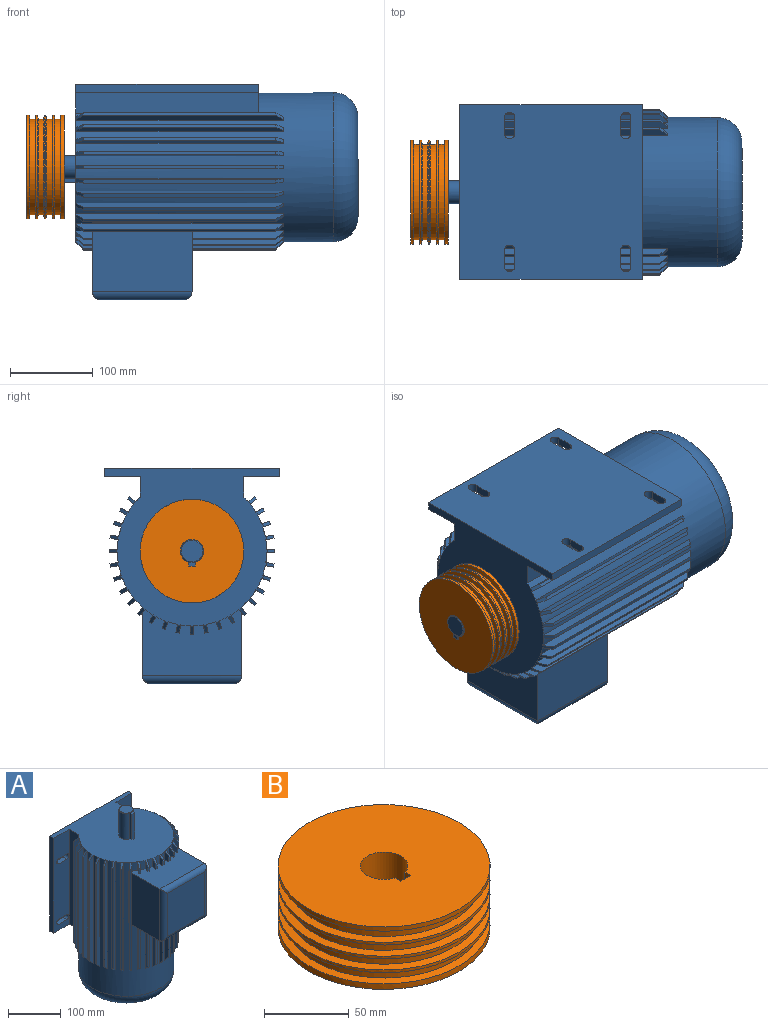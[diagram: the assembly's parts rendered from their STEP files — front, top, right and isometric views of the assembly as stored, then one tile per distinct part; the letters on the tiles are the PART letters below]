
ASSEMBLY  parts=2 mates=1
PART A: 242 faces, bbox 210.4x260.4x400.4 mm
  f0: plane 250x7.66mm, normal (0.77,-0.64,0), area 1729.1mm2, adj f30,f31,f53,f54,f55,f56,f57,f234
  f1: plane 250x7.66mm, normal (-0.77,-0.64,0), area 1729.1mm2, adj f2,f31,f54,f58,f59,f60,f61,f235
  f2: cylinder r=90mm len=20mm, axis (0,0,1), area 234.2mm2, adj f1,f3,f54,f235
  f3: plane 20x8.66mm, normal (0.87,0.5,0), area 159.5mm2, adj f2,f4,f54,f62,f235
  f4: plane 11x3.46mm, normal (0.5,-0.87,0), area 44mm2, adj f3,f5,f62,f235
  f5: plane 20x8.66mm, normal (-0.87,-0.5,0), area 159.5mm2, adj f4,f6,f54,f62,f235
  f6: cylinder r=90mm len=20mm, axis (0,0,1), area 234.2mm2, adj f5,f7,f54,f235
  f7: plane 20x9.4mm, normal (0.94,0.34,0), area 159.5mm2, adj f6,f8,f54,f63,f235
  f8: plane 11x3.76mm, normal (0.34,-0.94,0), area 44mm2, adj f7,f9,f63,f235
  f9: plane 20x9.4mm, normal (-0.94,-0.34,0), area 159.5mm2, adj f8,f10,f54,f63,f235
  f10: cylinder r=90mm len=20mm, axis (0,0,1), area 234.2mm2, adj f9,f11,f54,f235
  f11: plane 20x9.85mm, normal (0.98,0.17,0), area 159.5mm2, adj f10,f12,f54,f64,f235
  f12: plane 11x3.94mm, normal (0.17,-0.98,0), area 44mm2, adj f11,f13,f64,f235
  f13: plane 20x9.85mm, normal (-0.98,-0.17,0), area 159.5mm2, adj f12,f14,f54,f64,f235
  f14: cylinder r=90mm len=20mm, axis (0,0,1), area 234.2mm2, adj f13,f15,f54,f235
  f15: plane 20x10mm, normal (1,0,0), area 159.5mm2, adj f14,f16,f54,f65,f235
  f16: plane 11x4mm, normal (0,-1,0), area 44mm2, adj f15,f17,f65,f235
  f17: plane 20x10mm, normal (-1,0,0), area 159.5mm2, adj f16,f18,f54,f65,f235
  f18: cylinder r=90mm len=20mm, axis (0,0,1), area 234.2mm2, adj f17,f19,f54,f235
  f19: plane 20x9.85mm, normal (0.98,-0.17,0), area 159.5mm2, adj f18,f20,f54,f66,f235
  f20: plane 11x3.94mm, normal (-0.17,-0.98,0), area 44mm2, adj f19,f21,f66,f235
  f21: plane 20x9.85mm, normal (-0.98,0.17,0), area 159.5mm2, adj f20,f22,f54,f66,f235
  f22: cylinder r=90mm len=20mm, axis (0,0,1), area 234.2mm2, adj f21,f23,f54,f235
  f23: plane 20x9.4mm, normal (0.94,-0.34,0), area 159.5mm2, adj f22,f24,f54,f67,f235
  f24: plane 11x3.76mm, normal (-0.34,-0.94,0), area 44mm2, adj f23,f25,f67,f235
  f25: plane 20x9.4mm, normal (-0.94,0.34,0), area 159.5mm2, adj f24,f26,f54,f67,f235
  f26: cylinder r=90mm len=20mm, axis (0,0,1), area 234.2mm2, adj f25,f27,f54,f235
  f27: plane 20x8.66mm, normal (0.87,-0.5,0), area 159.5mm2, adj f26,f28,f54,f68,f235
  f28: plane 11x3.46mm, normal (-0.5,-0.87,0), area 44mm2, adj f27,f29,f68,f235
  f29: plane 20x8.66mm, normal (-0.87,0.5,0), area 159.5mm2, adj f28,f30,f54,f68,f235
  f30: cylinder r=90mm len=20mm, axis (0,0,1), area 234.2mm2, adj f0,f29,f54,f235
  f31: cylinder r=90mm len=310mm, axis (0,0,1), area 104737.7mm2, adj f0,f1,f32,f34,f35,f37,f38,f40
  f32: plane 110x8.66mm, normal (-0.87,0.5,0), area 1059.5mm2, adj f31,f33,f75,f107,f237
  f33: plane 101x3.46mm, normal (-0.5,-0.87,0), area 404mm2, adj f32,f34,f107,f237
  f34: plane 110x8.66mm, normal (0.87,-0.5,0), area 1059.5mm2, adj f31,f33,f75,f107,f237
  f35: plane 110x9.4mm, normal (-0.94,0.34,0), area 1059.5mm2, adj f31,f36,f74,f108,f237
  f36: plane 101x3.76mm, normal (-0.34,-0.94,0), area 404mm2, adj f35,f37,f108,f237
  f37: plane 110x9.4mm, normal (0.94,-0.34,0), area 1059.5mm2, adj f31,f36,f74,f108,f237
  f38: plane 110x9.85mm, normal (-0.98,0.17,0), area 1059.5mm2, adj f31,f39,f73,f109,f237
  f39: plane 101x3.94mm, normal (-0.17,-0.98,0), area 404mm2, adj f38,f40,f109,f237
  f40: plane 110x9.85mm, normal (0.98,-0.17,0), area 1059.5mm2, adj f31,f39,f73,f109,f237
  f41: plane 110x10mm, normal (-1,0,0), area 1059.5mm2, adj f31,f42,f72,f110,f237
  f42: plane 101x4mm, normal (0,-1,0), area 404mm2, adj f41,f43,f110,f237
  f43: plane 110x10mm, normal (1,0,0), area 1059.5mm2, adj f31,f42,f72,f110,f237
  f44: plane 110x9.85mm, normal (-0.98,-0.17,0), area 1059.5mm2, adj f31,f45,f145,f146,f237
  f45: plane 101x3.94mm, normal (0.17,-0.98,0), area 404mm2, adj f44,f46,f146,f237
  f46: plane 110x9.85mm, normal (0.98,0.17,0), area 1059.5mm2, adj f31,f45,f145,f146,f237
  f47: plane 110x9.4mm, normal (-0.94,-0.34,0), area 1059.5mm2, adj f31,f48,f144,f147,f237
  f48: plane 101x3.76mm, normal (0.34,-0.94,0), area 404mm2, adj f47,f49,f147,f237
  f49: plane 110x9.4mm, normal (0.94,0.34,0), area 1059.5mm2, adj f31,f48,f144,f147,f237
  f50: plane 110x8.66mm, normal (-0.87,-0.5,0), area 1059.5mm2, adj f31,f51,f143,f148,f237
  f51: plane 101x3.46mm, normal (0.5,-0.87,0), area 404mm2, adj f50,f52,f148,f237
  f52: plane 110x8.66mm, normal (0.87,0.5,0), area 1059.5mm2, adj f31,f51,f143,f148,f237
  f53: plane 3.71x3.34mm, normal (0,0,-1), area 3.9mm2, adj f0,f31,f57,f76
  f54: plane 210x190.98mm, normal (0,0,1), area 27976mm2, adj f0,f1,f2,f3,f5,f6,f7,f9
  f55: plane 9.47x9mm, normal (-0.45,-0.54,0.71), area 50.9mm2, adj f0,f54,f56,f76
  f56: plane 232x3.06mm, normal (-0.64,-0.77,0), area 928mm2, adj f0,f55,f57,f76
  f57: plane 9.47x9mm, normal (-0.45,-0.54,-0.71), area 50.9mm2, adj f0,f53,f56,f76
  f58: plane 232x3.06mm, normal (0.64,-0.77,0), area 928mm2, adj f1,f59,f61,f139
  f59: plane 9.47x9mm, normal (0.45,-0.54,0.71), area 50.9mm2, adj f1,f54,f58,f139
  f60: plane 3.71x3.34mm, normal (0,0,-1), area 3.9mm2, adj f1,f31,f61,f139
  f61: plane 9.47x9mm, normal (0.45,-0.54,-0.71), area 50.9mm2, adj f1,f58,f60,f139
  f62: plane 9.79x9mm, normal (0.35,-0.61,0.71), area 50.9mm2, adj f3,f4,f5,f54
  f63: plane 9.83x9mm, normal (0.24,-0.66,0.71), area 50.9mm2, adj f7,f8,f9,f54
  f64: plane 9.56x9mm, normal (0.12,-0.7,0.71), area 50.9mm2, adj f11,f12,f13,f54
  f65: plane 9x9mm, normal (0,-0.71,0.71), area 50.9mm2, adj f15,f16,f17,f54
  f66: plane 9.56x9mm, normal (-0.12,-0.7,0.71), area 50.9mm2, adj f19,f20,f21,f54
  f67: plane 9.83x9mm, normal (-0.24,-0.66,0.71), area 50.9mm2, adj f23,f24,f25,f54
  f68: plane 9.79x9mm, normal (-0.35,-0.61,0.71), area 50.9mm2, adj f27,f28,f29,f54
  f69: plane 220x25mm, normal (-1,0,0), area 5500mm2, adj f31,f54,f70,f170
  f70: plane 210x35mm, normal (0,0,-1), area 3072mm2, adj f31,f69,f111,f166,f167,f168,f169,f170
  f71: torus R=60mm, axis (0,0,1), area 23420.2mm2, adj f31,f173
  f72: plane 4x1mm, normal (0,0,-1), area 3.9mm2, adj f31,f41,f43,f110
  f73: plane 4.11x1.68mm, normal (0,0,-1), area 3.9mm2, adj f31,f38,f40,f109
  f74: plane 4.1x2.31mm, normal (0,0,-1), area 3.9mm2, adj f31,f35,f37,f108
  f75: plane 3.96x2.87mm, normal (0,0,-1), area 3.9mm2, adj f31,f32,f34,f107
  f76: plane 250x7.66mm, normal (-0.77,0.64,0), area 2301.1mm2, adj f31,f53,f54,f55,f56,f57,f77,f78
  f77: plane 1.31x0.63mm, normal (0,0,-1), area 0.4mm2, adj f31,f76,f78
  f78: plane 120x1.31mm, normal (-1,0,0), area 157.4mm2, adj f31,f76,f77,f79
  f79: plane 1.31x0.63mm, normal (0,0,1), area 0.4mm2, adj f31,f76,f78
  f80: plane 250x7.66mm, normal (0.64,-0.77,0), area 2419mm2, adj f31,f54,f81,f156,f174,f175
  f81: plane 3.71x3.34mm, normal (0,0,-1), area 3.9mm2, adj f31,f80,f82,f175
  f82: plane 250x7.66mm, normal (-0.64,0.77,0), area 2419mm2, adj f31,f54,f81,f156,f174,f175
  f83: plane 250x8.66mm, normal (0.5,-0.87,0), area 2419mm2, adj f31,f54,f84,f155,f176,f177
  f84: plane 3.96x2.87mm, normal (0,0,-1), area 3.9mm2, adj f31,f83,f85,f177
  f85: plane 250x8.66mm, normal (-0.5,0.87,0), area 2419mm2, adj f31,f54,f84,f155,f176,f177
  f86: plane 250x9.4mm, normal (0.34,-0.94,0), area 2419mm2, adj f31,f54,f87,f154,f178,f179
  f87: plane 4.1x2.31mm, normal (0,0,-1), area 3.9mm2, adj f31,f86,f88,f179
  f88: plane 250x9.4mm, normal (-0.34,0.94,0), area 2419mm2, adj f31,f54,f87,f154,f178,f179
  f89: plane 250x9.85mm, normal (0.17,-0.98,0), area 2419mm2, adj f31,f54,f90,f153,f180,f181
  f90: plane 4.11x1.68mm, normal (0,0,-1), area 3.9mm2, adj f31,f89,f91,f181
  f91: plane 250x9.85mm, normal (-0.17,0.98,0), area 2419mm2, adj f31,f54,f90,f153,f180,f181
  f92: plane 250x10mm, normal (0,-1,0), area 2419mm2, adj f31,f54,f93,f152,f182,f183
  f93: plane 4x1mm, normal (0,0,-1), area 3.9mm2, adj f31,f92,f94,f183
  f94: plane 250x10mm, normal (0,1,0), area 2419mm2, adj f31,f54,f93,f152,f182,f183
  f95: plane 250x9.85mm, normal (-0.17,-0.98,0), area 2419mm2, adj f31,f54,f96,f151,f184,f185
  f96: plane 4.11x1.68mm, normal (0,0,-1), area 3.9mm2, adj f31,f95,f97,f185
  f97: plane 250x9.85mm, normal (0.17,0.98,0), area 2419mm2, adj f31,f54,f96,f151,f184,f185
  f98: plane 250x9.4mm, normal (-0.34,-0.94,0), area 2419mm2, adj f31,f54,f99,f150,f186,f187
  f99: plane 4.1x2.31mm, normal (0,0,-1), area 3.9mm2, adj f31,f98,f100,f187
  f100: plane 250x9.4mm, normal (0.34,0.94,0), area 2419mm2, adj f31,f54,f99,f150,f186,f187
  f101: plane 250x8.66mm, normal (-0.5,-0.87,0), area 2419mm2, adj f31,f54,f102,f149,f188,f189
  f102: plane 3.96x2.87mm, normal (0,0,-1), area 3.9mm2, adj f31,f101,f103,f189
  f103: plane 250x8.66mm, normal (0.5,0.87,0), area 2419mm2, adj f31,f54,f102,f149,f188,f189
  f104: plane 250x7.66mm, normal (-0.64,-0.77,0), area 2419mm2, adj f31,f54,f105,f171,f190,f191
  f105: plane 3.71x3.34mm, normal (0,0,-1), area 3.9mm2, adj f31,f104,f106,f191
  f106: plane 250x7.66mm, normal (0.64,0.77,0), area 2419mm2, adj f31,f54,f105,f171,f190,f191
  f107: plane 9.79x9mm, normal (-0.35,-0.61,-0.71), area 50.9mm2, adj f32,f33,f34,f75
  f108: plane 9.83x9mm, normal (-0.24,-0.66,-0.71), area 50.9mm2, adj f35,f36,f37,f74
  f109: plane 9.56x9mm, normal (-0.12,-0.7,-0.71), area 50.9mm2, adj f38,f39,f40,f73
  f110: plane 9x9mm, normal (0,-0.71,-0.71), area 50.9mm2, adj f41,f42,f43,f72
  f111: plane 220x25mm, normal (1,0,0), area 5500mm2, adj f31,f54,f70,f166
  f112: plane 250x7.66mm, normal (-0.64,0.77,0), area 2419mm2, adj f31,f54,f113,f165,f192,f193
  f113: plane 3.71x3.34mm, normal (0,0,-1), area 3.9mm2, adj f31,f112,f114,f193
  f114: plane 250x7.66mm, normal (0.64,-0.77,0), area 2419mm2, adj f31,f54,f113,f165,f192,f193
  f115: plane 250x8.66mm, normal (-0.5,0.87,0), area 2419mm2, adj f31,f54,f116,f164,f194,f195
  f116: plane 3.96x2.87mm, normal (0,0,-1), area 3.9mm2, adj f31,f115,f117,f195
  f117: plane 250x8.66mm, normal (0.5,-0.87,0), area 2419mm2, adj f31,f54,f116,f164,f194,f195
  f118: plane 250x9.4mm, normal (-0.34,0.94,0), area 2419mm2, adj f31,f54,f119,f163,f196,f197
  f119: plane 4.1x2.31mm, normal (0,0,-1), area 3.9mm2, adj f31,f118,f120,f197
  f120: plane 250x9.4mm, normal (0.34,-0.94,0), area 2419mm2, adj f31,f54,f119,f163,f196,f197
  f121: plane 250x9.85mm, normal (-0.17,0.98,0), area 2419mm2, adj f31,f54,f122,f162,f198,f199
  f122: plane 4.11x1.68mm, normal (0,0,-1), area 3.9mm2, adj f31,f121,f123,f199
  f123: plane 250x9.85mm, normal (0.17,-0.98,0), area 2419mm2, adj f31,f54,f122,f162,f198,f199
  f124: plane 250x10mm, normal (0,1,0), area 2419mm2, adj f31,f54,f125,f161,f200,f201
  f125: plane 4x1mm, normal (0,0,-1), area 3.9mm2, adj f31,f124,f126,f201
  f126: plane 250x10mm, normal (0,-1,0), area 2419mm2, adj f31,f54,f125,f161,f200,f201
  f127: plane 250x9.85mm, normal (0.17,0.98,0), area 2419mm2, adj f31,f54,f128,f160,f202,f203
  f128: plane 4.11x1.68mm, normal (0,0,-1), area 3.9mm2, adj f31,f127,f129,f203
  f129: plane 250x9.85mm, normal (-0.17,-0.98,0), area 2419mm2, adj f31,f54,f128,f160,f202,f203
  f130: plane 250x9.4mm, normal (0.34,0.94,0), area 2419mm2, adj f31,f54,f131,f159,f204,f205
  f131: plane 4.1x2.31mm, normal (0,0,-1), area 3.9mm2, adj f31,f130,f132,f205
  f132: plane 250x9.4mm, normal (-0.34,-0.94,0), area 2419mm2, adj f31,f54,f131,f159,f204,f205
  f133: plane 250x8.66mm, normal (0.5,0.87,0), area 2419mm2, adj f31,f54,f134,f158,f206,f207
  f134: plane 3.96x2.87mm, normal (0,0,-1), area 3.9mm2, adj f31,f133,f135,f207
  f135: plane 250x8.66mm, normal (-0.5,-0.87,0), area 2419mm2, adj f31,f54,f134,f158,f206,f207
  f136: plane 250x7.66mm, normal (0.64,0.77,0), area 2419mm2, adj f31,f54,f137,f157,f208,f209
  f137: plane 3.71x3.34mm, normal (0,0,-1), area 3.9mm2, adj f31,f136,f138,f209
  f138: plane 250x7.66mm, normal (-0.64,-0.77,0), area 2419mm2, adj f31,f54,f137,f157,f208,f209
  f139: plane 250x7.66mm, normal (0.77,0.64,0), area 2301.1mm2, adj f31,f54,f58,f59,f60,f61,f140,f141
  f140: plane 1.31x0.63mm, normal (0,0,1), area 0.4mm2, adj f31,f139,f141
  f141: plane 120x1.31mm, normal (1,0,0), area 157.4mm2, adj f31,f139,f140,f142
  f142: plane 1.31x0.63mm, normal (0,0,-1), area 0.4mm2, adj f31,f139,f141
  f143: plane 3.96x2.87mm, normal (0,0,-1), area 3.9mm2, adj f31,f50,f52,f148
  f144: plane 4.1x2.31mm, normal (0,0,-1), area 3.9mm2, adj f31,f47,f49,f147
  f145: plane 4.11x1.68mm, normal (0,0,-1), area 3.9mm2, adj f31,f44,f46,f146
  f146: plane 9.56x9mm, normal (0.12,-0.7,-0.71), area 50.9mm2, adj f44,f45,f46,f145
  f147: plane 9.83x9mm, normal (0.24,-0.66,-0.71), area 50.9mm2, adj f47,f48,f49,f144
  f148: plane 9.79x9mm, normal (0.35,-0.61,-0.71), area 50.9mm2, adj f50,f51,f52,f143
  f149: plane 9.79x9mm, normal (-0.61,0.35,0.71), area 50.9mm2, adj f54,f101,f103,f188
  f150: plane 9.83x9mm, normal (-0.66,0.24,0.71), area 50.9mm2, adj f54,f98,f100,f186
  f151: plane 9.56x9mm, normal (-0.7,0.12,0.71), area 50.9mm2, adj f54,f95,f97,f184
  f152: plane 9x9mm, normal (-0.71,0,0.71), area 50.9mm2, adj f54,f92,f94,f182
  f153: plane 9.56x9mm, normal (-0.7,-0.12,0.71), area 50.9mm2, adj f54,f89,f91,f180
  f154: plane 9.83x9mm, normal (-0.66,-0.24,0.71), area 50.9mm2, adj f54,f86,f88,f178
  f155: plane 9.79x9mm, normal (-0.61,-0.35,0.71), area 50.9mm2, adj f54,f83,f85,f176
  f156: plane 9.47x9mm, normal (-0.54,-0.45,0.71), area 50.9mm2, adj f54,f80,f82,f174
  f157: plane 9.47x9mm, normal (0.54,-0.45,0.71), area 50.9mm2, adj f54,f136,f138,f208
  f158: plane 9.79x9mm, normal (0.61,-0.35,0.71), area 50.9mm2, adj f54,f133,f135,f206
  f159: plane 9.83x9mm, normal (0.66,-0.24,0.71), area 50.9mm2, adj f54,f130,f132,f204
  f160: plane 9.56x9mm, normal (0.7,-0.12,0.71), area 50.9mm2, adj f54,f127,f129,f202
  f161: plane 9x9mm, normal (0.71,0,0.71), area 50.9mm2, adj f54,f124,f126,f200
  f162: plane 9.56x9mm, normal (0.7,0.12,0.71), area 50.9mm2, adj f54,f121,f123,f198
  f163: plane 9.83x9mm, normal (0.66,0.24,0.71), area 50.9mm2, adj f54,f118,f120,f196
  f164: plane 9.79x9mm, normal (0.61,0.35,0.71), area 50.9mm2, adj f54,f115,f117,f194
  f165: plane 9.47x9mm, normal (0.54,0.45,0.71), area 50.9mm2, adj f54,f112,f114,f192
  f166: plane 220x42.75mm, normal (0,-1,0), area 8698.9mm2, adj f54,f70,f111,f167,f210,f211,f212,f213
  f167: plane 220x10mm, normal (1,0,0), area 2200mm2, adj f54,f70,f166,f168
  f168: plane 220x210mm, normal (0,1,0), area 44787.6mm2, adj f54,f70,f167,f169,f210,f211,f212,f213
  f169: plane 220x10mm, normal (-1,0,0), area 2200mm2, adj f54,f70,f168,f170
  f170: plane 220x42.75mm, normal (0,-1,0), area 8698.9mm2, adj f54,f69,f70,f169,f218,f219,f220,f221
  f171: plane 9.47x9mm, normal (-0.54,0.45,0.71), area 50.9mm2, adj f54,f104,f106,f190
  f172: cylinder r=14mm len=59mm, axis (0,0,1), area 4711.2mm2, adj f54,f226,f230,f232
  f173: plane 120x120mm, normal (0,0,-1), area 11309.7mm2, adj f71
  f174: plane 232x3.06mm, normal (-0.77,-0.64,0), area 928mm2, adj f80,f82,f156,f175
  f175: plane 9.47x9mm, normal (-0.54,-0.45,-0.71), area 50.9mm2, adj f80,f81,f82,f174
  f176: plane 232x3.46mm, normal (-0.87,-0.5,0), area 928mm2, adj f83,f85,f155,f177
  f177: plane 9.79x9mm, normal (-0.61,-0.35,-0.71), area 50.9mm2, adj f83,f84,f85,f176
  f178: plane 232x3.76mm, normal (-0.94,-0.34,0), area 928mm2, adj f86,f88,f154,f179
  f179: plane 9.83x9mm, normal (-0.66,-0.24,-0.71), area 50.9mm2, adj f86,f87,f88,f178
  f180: plane 232x3.94mm, normal (-0.98,-0.17,0), area 928mm2, adj f89,f91,f153,f181
  f181: plane 9.56x9mm, normal (-0.7,-0.12,-0.71), area 50.9mm2, adj f89,f90,f91,f180
  f182: plane 232x4mm, normal (-1,0,0), area 928mm2, adj f92,f94,f152,f183
  f183: plane 9x9mm, normal (-0.71,0,-0.71), area 50.9mm2, adj f92,f93,f94,f182
  f184: plane 232x3.94mm, normal (-0.98,0.17,0), area 928mm2, adj f95,f97,f151,f185
  f185: plane 9.56x9mm, normal (-0.7,0.12,-0.71), area 50.9mm2, adj f95,f96,f97,f184
  f186: plane 232x3.76mm, normal (-0.94,0.34,0), area 928mm2, adj f98,f100,f150,f187
  f187: plane 9.83x9mm, normal (-0.66,0.24,-0.71), area 50.9mm2, adj f98,f99,f100,f186
  f188: plane 232x3.46mm, normal (-0.87,0.5,0), area 928mm2, adj f101,f103,f149,f189
  f189: plane 9.79x9mm, normal (-0.61,0.35,-0.71), area 50.9mm2, adj f101,f102,f103,f188
  f190: plane 232x3.06mm, normal (-0.77,0.64,0), area 928mm2, adj f104,f106,f171,f191
  f191: plane 9.47x9mm, normal (-0.54,0.45,-0.71), area 50.9mm2, adj f104,f105,f106,f190
  f192: plane 232x3.06mm, normal (0.77,0.64,0), area 928mm2, adj f112,f114,f165,f193
  f193: plane 9.47x9mm, normal (0.54,0.45,-0.71), area 50.9mm2, adj f112,f113,f114,f192
  f194: plane 232x3.46mm, normal (0.87,0.5,0), area 928mm2, adj f115,f117,f164,f195
  f195: plane 9.79x9mm, normal (0.61,0.35,-0.71), area 50.9mm2, adj f115,f116,f117,f194
  f196: plane 232x3.76mm, normal (0.94,0.34,0), area 928mm2, adj f118,f120,f163,f197
  f197: plane 9.83x9mm, normal (0.66,0.24,-0.71), area 50.9mm2, adj f118,f119,f120,f196
  f198: plane 232x3.94mm, normal (0.98,0.17,0), area 928mm2, adj f121,f123,f162,f199
  f199: plane 9.56x9mm, normal (0.7,0.12,-0.71), area 50.9mm2, adj f121,f122,f123,f198
  f200: plane 232x4mm, normal (1,0,0), area 928mm2, adj f124,f126,f161,f201
  f201: plane 9x9mm, normal (0.71,0,-0.71), area 50.9mm2, adj f124,f125,f126,f200
  f202: plane 232x3.94mm, normal (0.98,-0.17,0), area 928mm2, adj f127,f129,f160,f203
  f203: plane 9.56x9mm, normal (0.7,-0.12,-0.71), area 50.9mm2, adj f127,f128,f129,f202
  f204: plane 232x3.76mm, normal (0.94,-0.34,0), area 928mm2, adj f130,f132,f159,f205
  f205: plane 9.83x9mm, normal (0.66,-0.24,-0.71), area 50.9mm2, adj f130,f131,f132,f204
  f206: plane 232x3.46mm, normal (0.87,-0.5,0), area 928mm2, adj f133,f135,f158,f207
  f207: plane 9.79x9mm, normal (0.61,-0.35,-0.71), area 50.9mm2, adj f133,f134,f135,f206
  f208: plane 232x3.06mm, normal (0.77,-0.64,0), area 928mm2, adj f136,f138,f157,f209
  f209: plane 9.47x9mm, normal (0.54,-0.45,-0.71), area 50.9mm2, adj f136,f137,f138,f208
  f210: cylinder r=6mm len=12mm, axis (0,1,0), area 188.5mm2, adj f166,f168,f211,f213
  f211: plane 20x10mm, normal (0,0,-1), area 200mm2, adj f166,f168,f210,f212
  f212: cylinder r=6mm len=12mm, axis (0,1,0), area 188.5mm2, adj f166,f168,f211,f213
  f213: plane 20x10mm, normal (0,0,1), area 200mm2, adj f166,f168,f210,f212
  f214: plane 20x10mm, normal (0,0,-1), area 200mm2, adj f166,f168,f215,f217
  f215: cylinder r=6mm len=12mm, axis (0,1,0), area 188.5mm2, adj f166,f168,f214,f216
  f216: plane 20x10mm, normal (0,0,1), area 200mm2, adj f166,f168,f215,f217
  f217: cylinder r=6mm len=12mm, axis (0,1,0), area 188.5mm2, adj f166,f168,f214,f216
  f218: plane 20x10mm, normal (0,0,-1), area 200mm2, adj f168,f170,f219,f221
  f219: cylinder r=6mm len=12mm, axis (0,1,0), area 188.5mm2, adj f168,f170,f218,f220
  f220: plane 20x10mm, normal (0,0,1), area 200mm2, adj f168,f170,f219,f221
  f221: cylinder r=6mm len=12mm, axis (0,1,0), area 188.5mm2, adj f168,f170,f218,f220
  f222: plane 20x10mm, normal (0,0,-1), area 200mm2, adj f168,f170,f223,f225
  f223: cylinder r=6mm len=12mm, axis (0,1,0), area 188.5mm2, adj f168,f170,f222,f224
  f224: plane 20x10mm, normal (0,0,1), area 200mm2, adj f168,f170,f223,f225
  f225: cylinder r=6mm len=12mm, axis (0,1,0), area 188.5mm2, adj f168,f170,f222,f224
  f226: cone r=1mm half-angle=45deg, axis (0,0,-1), area 116.7mm2, adj f172,f227,f229
  f227: plane 26x26mm, normal (0,0,1), area 530.9mm2, adj f226
  f228: plane 8x4.58mm, normal (0,0,1), area 36.7mm2, adj f229,f230,f231,f232
  f229: plane 8.42x1.42mm, normal (0,1,0), area 4.9mm2, adj f226,f228,f230,f232
  f230: plane 60x4.58mm, normal (-1,0,0), area 275mm2, adj f54,f172,f228,f229,f231
  f231: plane 60x8mm, normal (0,-1,0), area 480mm2, adj f54,f228,f230,f232
  f232: plane 60x4.58mm, normal (1,0,0), area 275mm2, adj f54,f172,f228,f229,f231
  f233: plane 100x100mm, normal (0,-1,0), area 10000mm2, adj f238,f239,f240,f241
  f234: plane 120x75.38mm, normal (-1,0,0), area 9046mm2, adj f0,f235,f237,f241
  f235: plane 120x79.79mm, normal (0,0,1), area 7757.1mm2, adj f0,f1,f2,f3,f4,f5,f6,f7
  f236: plane 120x75.38mm, normal (1,0,0), area 9046mm2, adj f1,f235,f237,f239
  f237: plane 120x79.79mm, normal (0,0,-1), area 7757.1mm2, adj f0,f1,f31,f32,f33,f34,f35,f36
  f238: cylinder r=10mm len=120mm, axis (-1,0,0), area 1770.8mm2, adj f233,f235,f239,f241
  f239: cylinder r=10mm len=120mm, axis (0,0,-1), area 1770.6mm2, adj f233,f236,f238,f240
  f240: cylinder r=10mm len=120mm, axis (1,0,0), area 1770.8mm2, adj f233,f237,f239,f241
  f241: cylinder r=10mm len=120mm, axis (0,0,1), area 1770.6mm2, adj f233,f234,f238,f240
PART B: 23 faces, bbox 125x125x45 mm
  f0: cylinder r=62.5mm len=125mm, axis (0,0,1), area 1570.8mm2, adj f9,f20
  f1: cylinder r=62.5mm len=125mm, axis (0,0,1), area 785.4mm2, adj f17,f22
  f2: cylinder r=62.5mm len=125mm, axis (0,0,1), area 785.4mm2, adj f14,f19
  f3: cylinder r=62.5mm len=125mm, axis (0,0,1), area 785.4mm2, adj f11,f16
  f4: cylinder r=14mm len=45mm, axis (0,0,1), area 3593.3mm2, adj f5,f7,f9,f10
  f5: plane 45x4.58mm, normal (-1,0,0), area 206.3mm2, adj f4,f6,f9,f10
  f6: plane 45x8mm, normal (0,1,0), area 360mm2, adj f5,f7,f9,f10
  f7: plane 45x4.58mm, normal (1,0,0), area 206.3mm2, adj f4,f6,f9,f10
  f8: cylinder r=62.5mm len=125mm, axis (0,0,1), area 1178.1mm2, adj f10,f13
  f9: plane 125x125mm, normal (0,0,-1), area 11622.6mm2, adj f0,f4,f5,f6,f7
  f10: plane 125x125mm, normal (0,0,1), area 11622.6mm2, adj f4,f5,f6,f7,f8
  f11: cone r=65.5mm half-angle=82.5deg, axis (0,0,-1), area 1901.2mm2, adj f3,f12
  f12: cylinder r=57.5mm len=115mm, axis (0,0,1), area 2414.6mm2, adj f11,f13
  f13: cone r=57.5mm half-angle=82.5deg, axis (0,0,1), area 1901.2mm2, adj f8,f12
  f14: cone r=65.5mm half-angle=82.5deg, axis (0,0,-1), area 1901.2mm2, adj f2,f15
  f15: cylinder r=57.5mm len=115mm, axis (0,0,1), area 2414.6mm2, adj f14,f16
  f16: cone r=57.5mm half-angle=82.5deg, axis (0,0,1), area 1901.2mm2, adj f3,f15
  f17: cone r=65.5mm half-angle=82.5deg, axis (0,0,-1), area 1901.2mm2, adj f1,f18
  f18: cylinder r=57.5mm len=115mm, axis (0,0,1), area 2414.6mm2, adj f17,f19
  f19: cone r=57.5mm half-angle=82.5deg, axis (0,0,1), area 1901.2mm2, adj f2,f18
  f20: cone r=65.5mm half-angle=82.5deg, axis (0,0,-1), area 1901.2mm2, adj f0,f21
  f21: cylinder r=57.5mm len=115mm, axis (0,0,1), area 2414.6mm2, adj f20,f22
  f22: cone r=57.5mm half-angle=82.5deg, axis (0,0,1), area 1901.2mm2, adj f1,f21
PLACE A rot(axis=(0.58,-0.58,-0.58),120deg) t=(-471.09,-8.77,-202.32)mm fixed
PLACE B rot(axis=(0.58,-0.58,-0.58),120deg) t=(-470.09,-8.77,-202.32)mm
MATE fastened B.f4 <-> A.f2  axis (-1,0,0) through (-530.09,-8.77,-202.32)mm
